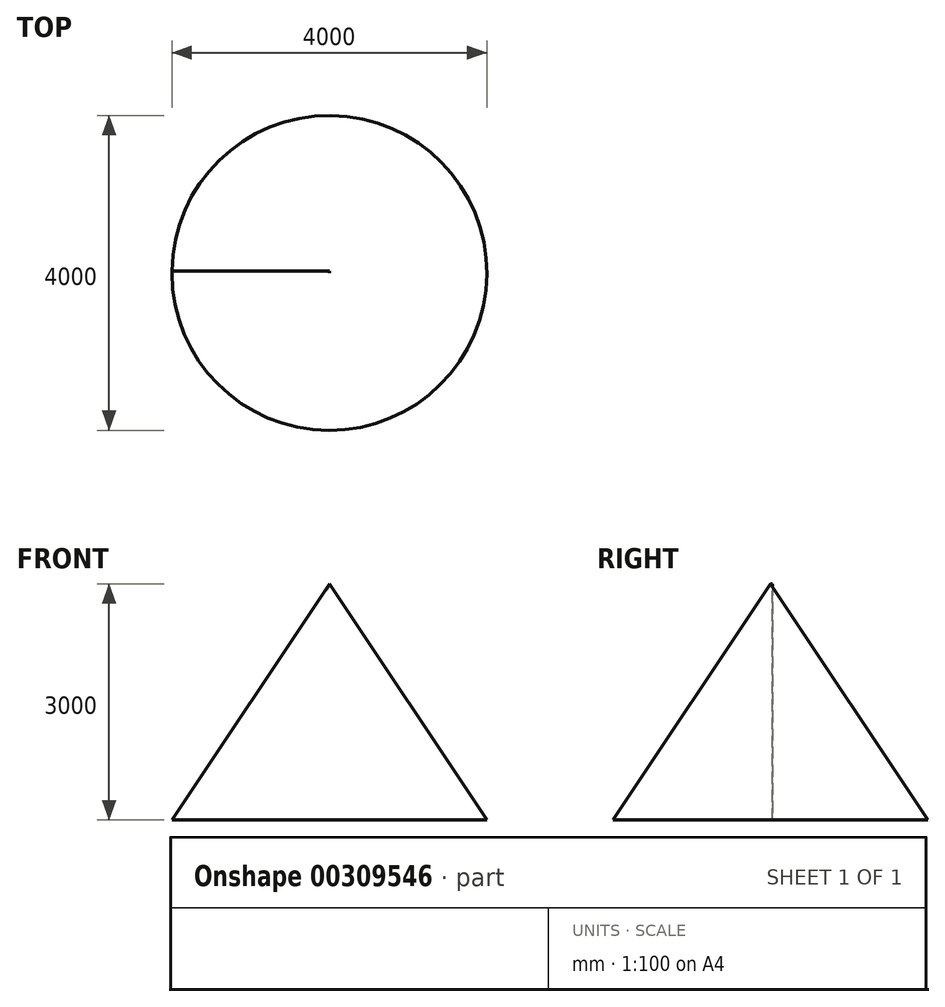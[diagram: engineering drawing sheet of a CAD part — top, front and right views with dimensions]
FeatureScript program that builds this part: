
annotation { "Feature Type Name" : "Feature", "Feature Type Description" : "" }
export const myFeature = defineFeature(function(context is Context, id is Id, definition is map)
    precondition{}
    {
        {
            var Q0;
            Q0=qCreatedBy(makeId("Front.planeOp"),FACE);
            var sketch = newSketch(context, id + "F0", { "sketchPlane" : qUnion([Q0])});
            skLineSegment(sketch, "E0", {"start": v(0, 0) * mm, "end": v(0, 3000) * mm});
            skLineSegment(sketch, "E1", {"start": v(0, 3000) * mm, "end": v(-2000, 0) * mm});
            skLineSegment(sketch, "E2", {"start": v(-2000, 0) * mm, "end": v(0, 0) * mm});
            skSolve(sketch);
        }
        {
            var Q0;
            Q0 = qSketchRegion(id + "F0", true);
            extrude(context, id + "F1", {"entities" : qUnion([Q0]), "depth" : 25 * mm});
        }
        {
            var Q0;
            Q0=makeQuery(id+"F1.opExtrude","CAP_FACE",FACE,{"disambiguationData":[OSD([sQuery(id+"F0.wireOp",EDGE,"E0"),sQuery(id+"F0.wireOp",EDGE,"E1"),sQuery(id+"F0.wireOp",EDGE,"E2")])],"isStart":false});
            var Q1;
            Q1=makeQuery(id+"F1.opExtrude","CAP_EDGE",EDGE,{"disambiguationData":[OSD([sQuery(id+"F0.wireOp",EDGE,"E0")])],"isStart":false});
            revolve(context, id + "F2", {"operationType" : NewBodyOperationType.ADD, "entities" : qUnion([Q0]), "axis" : qUnion([Q1]), "revolveType" : RevolveType.FULL});
        }
    });
